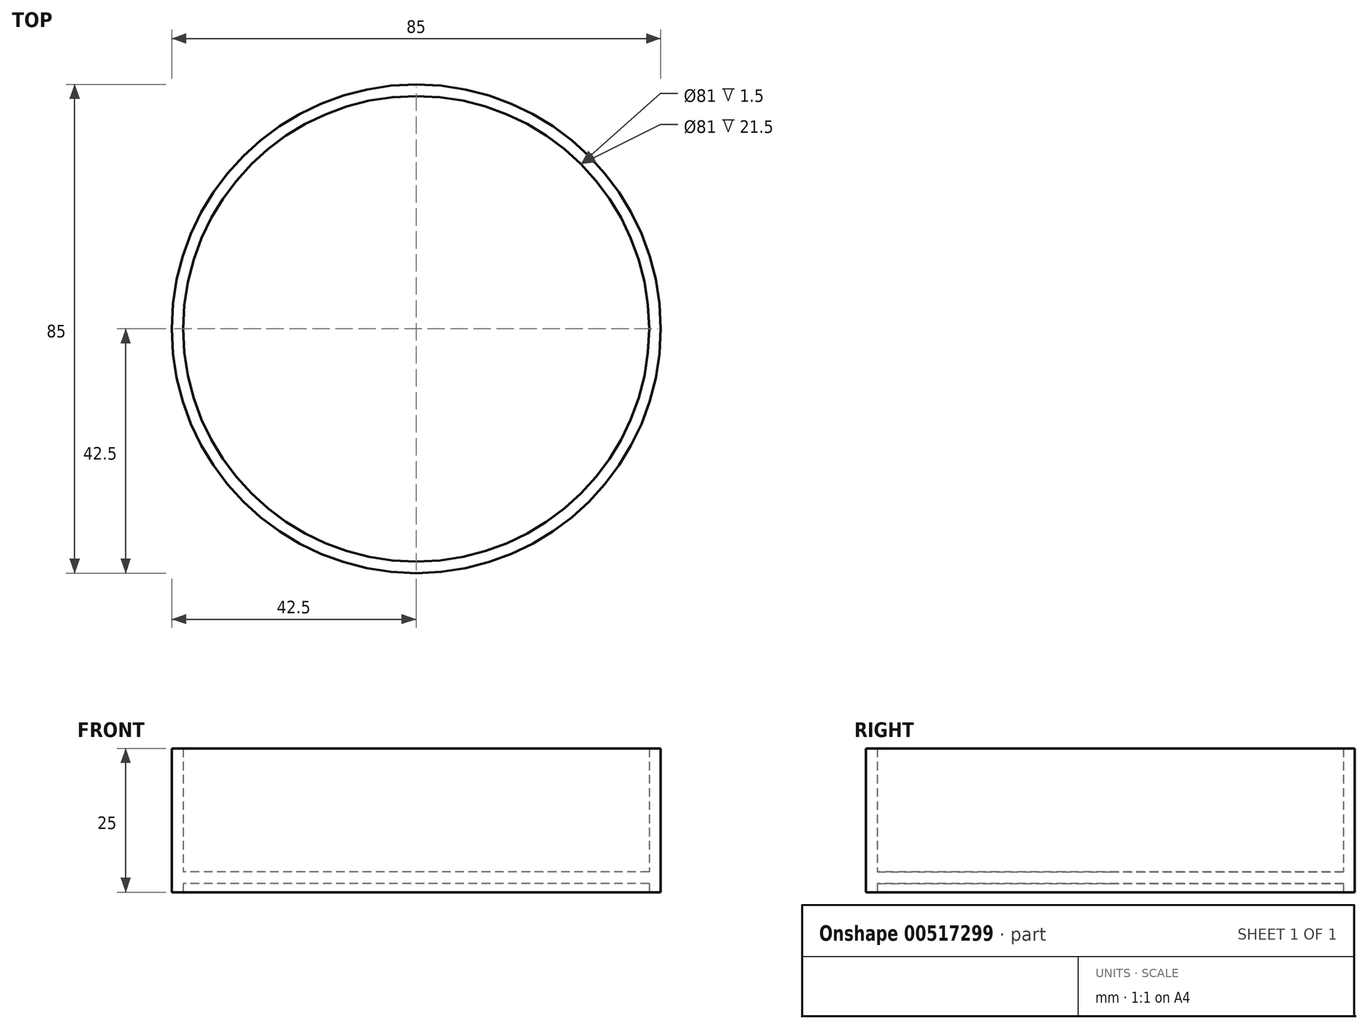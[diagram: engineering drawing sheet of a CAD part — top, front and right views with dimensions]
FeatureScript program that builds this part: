
annotation { "Feature Type Name" : "Feature", "Feature Type Description" : "" }
export const myFeature = defineFeature(function(context is Context, id is Id, definition is map)
    precondition{}
    {
        {
            var Q0;
            Q0=qCreatedBy(makeId("Top.planeOp"),FACE);
            var sketch = newSketch(context, id + "F0", { "sketchPlane" : qUnion([Q0])});
            skCircle(sketch, "E0", {"center": v(0, 0) * mm, "radius": 42.13 * mm});
            skSolve(sketch);
        }
        {
            var Q0;
            Q0 = qSketchRegion(id + "F0", true);
            extrude(context, id + "F1", {"entities" : qUnion([Q0]), "depth" : 2 * mm, "offsetDistance" : 25 * mm});
        }
        {
            var Q0;
            Q0=makeQuery(id+"F1.opExtrude","SWEPT_BODY",BODY,{"disambiguationData":[OSD([sQuery(id+"F0.wireOp",EDGE,"E0")])]});
            transform(context, id + "F2", {"entities" : qUnion([Q0]), "transformType" : TransformType.TRANSLATION_3D, "dx" : 0 * mm, "dy" : 0 * mm, "dz" : 1.5 * mm, "makeCopy" : false});
        }
        {
            var Q0;
            Q0=qCreatedBy(makeId("Top.planeOp"),FACE);
            var sketch = newSketch(context, id + "F3", { "sketchPlane" : qUnion([Q0])});
            skCircle(sketch, "E1", {"center": v(0, 0) * mm, "radius": 40.5 * mm});
            skCircle(sketch, "E2", {"center": v(0, 0) * mm, "radius": 42.5 * mm});
            skSolve(sketch);
        }
        {
            var Q0;
            Q0 = qSketchRegion(id + "F3", true);
            extrude(context, id + "F4", {"entities" : qUnion([Q0]), "operationType" : NewBodyOperationType.ADD, "depth" : 25 * mm, "offsetDistance" : 25 * mm});
        }
    });
